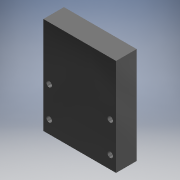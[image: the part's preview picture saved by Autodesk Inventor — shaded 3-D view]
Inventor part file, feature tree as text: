
AUTODESK INVENTOR PART (.ipt)
format: ipt  version: 2019 (Build 230136000, 136)  size: 103,424 bytes
history: native  units: mm (DEFAULTED — no unit token found)
features: extrude x2, sketch x2, plane x1, mirror x1
ambient origin geometry x8: Origin, YZ Plane, XZ Plane, XY Plane, X Axis, Y Axis, Z Axis, Center Point
bodies: Solid1 (feature_tree)
feature tree (6):
  extrude  "Extrusion1"  Depth=50.8mm
  extrude  "Extrusion2"  Depth=10.795mm
  plane  "Work Plane1"
  mirror  "Mirror1"
  sketch  "Sketch1"  dims[d0=38.1mm d1=50.8mm]
  sketch  "Sketch2"  dims[d2=10.795mm d3=0.0mm d4=3.048mm d5=3.048mm d6=16.002mm d7=6.731mm d8=2.921mm d9=2.921mm d10=6.35mm d11=0.0mm]
